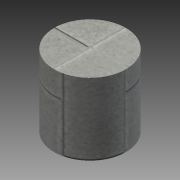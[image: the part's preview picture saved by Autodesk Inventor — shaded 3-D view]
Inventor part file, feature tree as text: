
AUTODESK INVENTOR PART (.ipt)
format: ipt  version: 2015 (Build 190159000, 159)  size: 93,184 bytes
history: native  units: in
note: dims shown in document units (in); Inventor stores cm internally (conversion verified against a paired STEP export)
features: extrude x1, sketch x1
ambient origin geometry x8: Origin, YZ Plane, XZ Plane, XY Plane, X Axis, Y Axis, Z Axis, Center Point
bodies: Solid1 (feature_tree)
feature tree (2):
  extrude  "Extrusion1"  Depth=12.0in TaperAngle=0.0deg
  sketch  "Sketch1"  dims[d0=12.0in d1=12.0in d2=0.0in]
